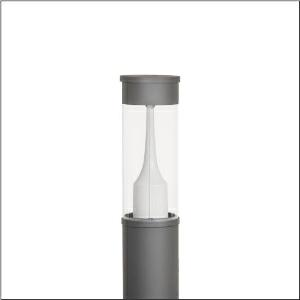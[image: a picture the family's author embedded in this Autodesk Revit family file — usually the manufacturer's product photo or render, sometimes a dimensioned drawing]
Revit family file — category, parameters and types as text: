
# Revit family: city-light_120_iq___p1_0a_5xa5285ff14h_303b
name_source: partatom
category: Lighting Fixtures
units: mm (PartAtom-declared; Revit-internal decimal feet)

## family parameters
Cut with Voids When Loaded = No
Host = Face
Light Source = No
Part Type = Normal
Room Calculation Point = No
Round Connector Dimension = Use Diameter
Shared = No

## types (1)
- --- (1 x LED, 1510 lm, 10.5 W, 3000K)
    Apparent Load = 11 VA
    CIE Flux Codes = 32 61 90 93 100
    Color Rendering = 70
    Color Temperature = 3000K
    Default Elevation = 1800 mm
    Description = City-Light 120 iQ, bollard luminaire, Module 540 iQ-SR, primary light control with 3 zone facetted reflector, of plastic, silver coated, highly specular, structured, primary optical cover: cover, of PMMA, transparent, light distribution: P1.0a, primary light characteristic: strongly asymmetric, LED, High Power LED, rated luminous flux: 1.510lm, luminous efficacy: 144lm/W, light colour: 730, colour temperature: 3000K, control gear: ECG iQ, control: Auto-Match, Temp-Guard, Lumen-Switch, Night-Set, Smart-Wire, Light-Fading, Desk-Remote (wireless, voltage-free reading and setting of iQ features in the workshop via application-optimized NFC function/RFID function), optimised constant luminous flux control (CLO 2.0), Street-Remote, presetting dimming logarithmic, with terminal, 6-pole, max. 2.5mm², mains connection: 230..240V, AC, 50/60Hz, start of lifetime: 11W, end of service life: 11W, reduction: 5W, luminaire housing, cylindrical, of extruded aluminium section, coated, Siteco® metallic grey (DB 702S), length: 1.200mm, diameter: 200mm, Module 540 iQ-SR, traffic white (RAL 9016), equipment: standard, protection rating (complete): IP54, insulation class (complete): insulation class II (safety insulation), certification: CE, ENEC, VDE, packaging unit: 1 piece

Light Distribution: P1.0a
    Height = 500 mm
    Lamp = 1 x LED
    Lamp Light Flux = 1510 lm
    Lamp Power = 10.5 W
    Lamp count = 1
    Length = 200 mm  [stored 0.656168 ft]
    Luminous efficacy = 144 lm/W
    Manufacturer = Siteco
    ModVariant = No
    Model = 5XA5285FF14H
    Mounting Place = Floor
    Mounting Type = Freestanding
    Number of Poles = 1
    OnlyDefault = Yes
    Power Factor = 1
    Product Name = City-Light 120 iQ | P1.0a
    Product group = bollard luminaire
    ProductGroupID = 1304
    Protection Class = Protection class II
    Protection Degree = IP 54
    RLX_Detail_Level = 1
    RLX_Emergency_Light_Flux = 0 lm
    RLX_Emergency_Type = 0
    RLX_Emergency_Type_DB = No
    RlxData = <blob elided: 52405 chars, md5=7f0fd8e4>
    Socket = socket
    Standby Power = 0 W
    System Light Flux = 1510 lm
    System Power = 11 W
    Type Comments = factory setting: luminous flux: 100 % | dim-lin: 254 | 419 mA
    Type Image = l_1006922.jpg
    URL = http://relux.com
    VarID = @adj_091919
    Voltage = 0 V
    Weight = 0.00 kg
    Width = 0 mm  [stored 0 ft]

note: [stored X ft] marks values corroborated as IEEE doubles in the binary element streams (Revit-internal decimal feet)

## geometry (parser evidence)
native form markers: Blend x4, Sweep x10
no freeform markers — native parametric forms only
